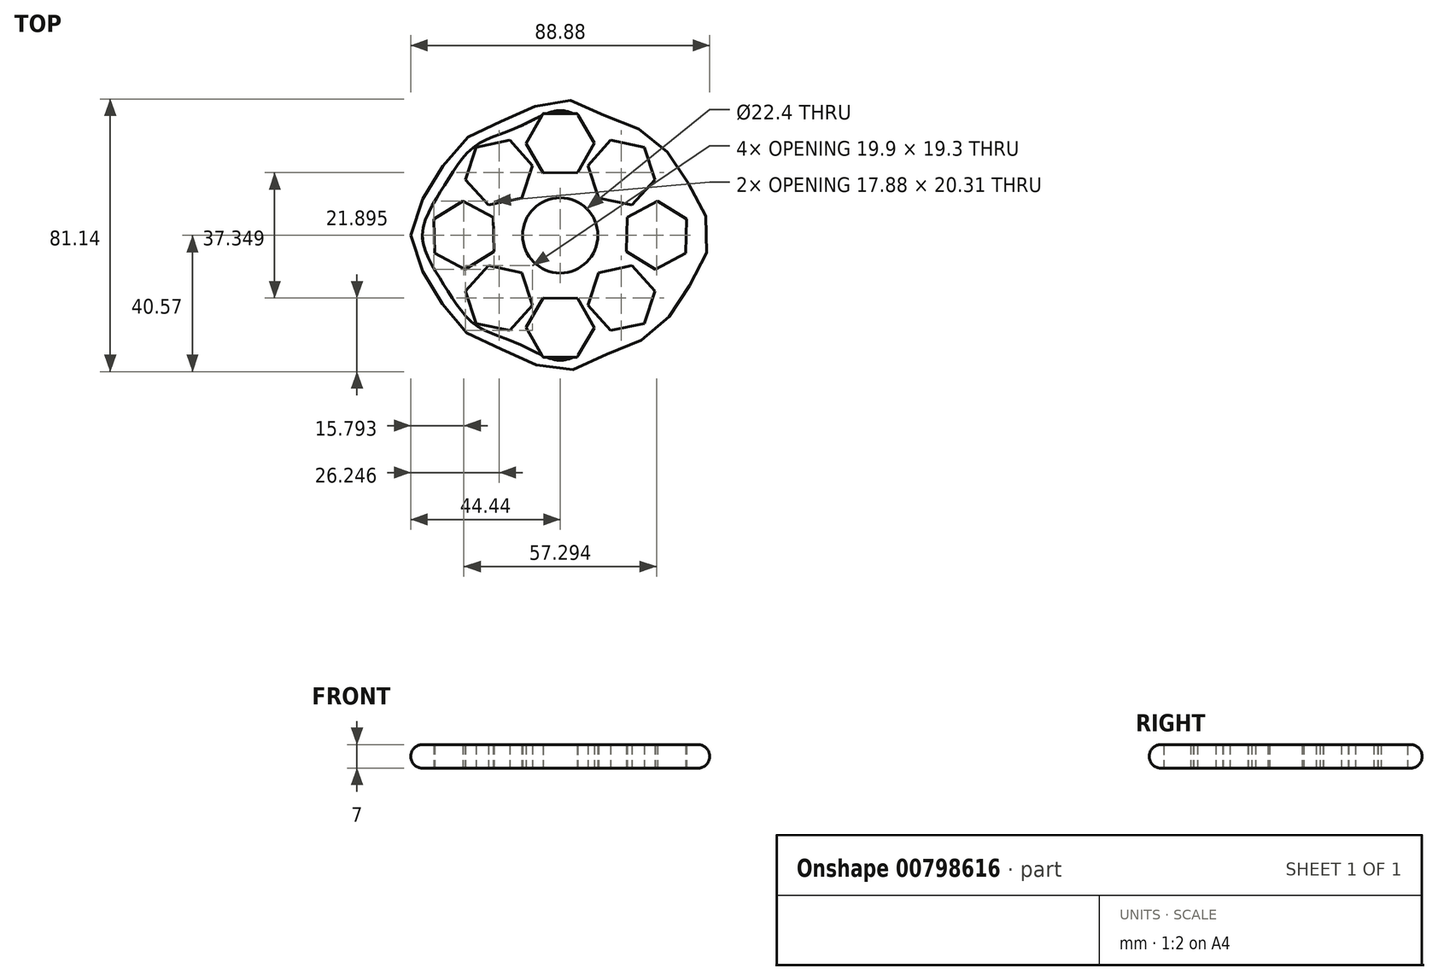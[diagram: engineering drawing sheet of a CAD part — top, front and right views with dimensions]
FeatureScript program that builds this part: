
annotation { "Feature Type Name" : "Feature", "Feature Type Description" : "" }
export const myFeature = defineFeature(function(context is Context, id is Id, definition is map)
    precondition{}
    {
        {
            var Q0;
            Q0=qCreatedBy(makeId("Top.planeOp"),FACE);
            var sketch = newSketch(context, id + "F0", { "sketchPlane" : qUnion([Q0])});
            skCircle(sketch, "E0", {"center": v(0, 0) * mm, "radius": 11.2 * mm});
            skCircle(sketch, "E1.cCircle", {"center": v(0, 27.46) * mm, "radius": 8.8 * mm});
            skLineSegment(sketch, "E1.0", {"start": v(10.16, 27.52) * mm, "end": v(5.14, 18.69) * mm});
            skLineSegment(sketch, "E1.1", {"start": v(5.14, 18.69) * mm, "end": v(-5.02, 18.62) * mm});
            skLineSegment(sketch, "E1.2", {"start": v(-5.02, 18.62) * mm, "end": v(-10.16, 27.4) * mm});
            skLineSegment(sketch, "E1.3", {"start": v(-10.16, 27.4) * mm, "end": v(-5.14, 36.22) * mm});
            skLineSegment(sketch, "E1.4", {"start": v(-5.14, 36.22) * mm, "end": v(5.02, 36.29) * mm});
            skLineSegment(sketch, "E1.5", {"start": v(5.02, 36.29) * mm, "end": v(10.16, 27.52) * mm});
            skCircle(sketch, "E2.MirrorC", {"center": v(0, -27.46) * mm, "radius": 8.8 * mm, "construction": true});
            skLineSegment(sketch, "E3.MirrorCS", {"start": v(-5.02, -18.62) * mm, "end": v(-10.16, -27.4) * mm});
            skLineSegment(sketch, "E4.MirrorCS", {"start": v(-10.16, -27.4) * mm, "end": v(-5.14, -36.22) * mm});
            skLineSegment(sketch, "E5.MirrorCS", {"start": v(-5.14, -36.22) * mm, "end": v(5.02, -36.29) * mm});
            skLineSegment(sketch, "E6.MirrorCS", {"start": v(5.02, -36.29) * mm, "end": v(10.16, -27.52) * mm});
            skLineSegment(sketch, "E7.MirrorCS", {"start": v(10.16, -27.52) * mm, "end": v(5.14, -18.69) * mm});
            skLineSegment(sketch, "E8.MirrorCS", {"start": v(5.14, -18.69) * mm, "end": v(-5.02, -18.62) * mm});
            skCircle(sketch, "E9.cCircle", {"center": v(28.65, 0) * mm, "radius": 8.8 * mm, "construction": true});
            skLineSegment(sketch, "E9.0", {"start": v(28.93, 10.16) * mm, "end": v(37.59, 4.83) * mm});
            skLineSegment(sketch, "E9.1", {"start": v(37.59, 4.83) * mm, "end": v(37.3, -5.33) * mm});
            skLineSegment(sketch, "E9.2", {"start": v(37.3, -5.33) * mm, "end": v(28.36, -10.16) * mm});
            skLineSegment(sketch, "E9.3", {"start": v(28.36, -10.16) * mm, "end": v(19.7, -4.83) * mm});
            skLineSegment(sketch, "E9.4", {"start": v(19.7, -4.83) * mm, "end": v(20, 5.33) * mm});
            skLineSegment(sketch, "E9.5", {"start": v(20, 5.33) * mm, "end": v(28.93, 10.16) * mm});
            skCircle(sketch, "E10.MirrorC", {"center": v(-28.65, 0) * mm, "radius": 8.8 * mm});
            skLineSegment(sketch, "E11.MirrorCS", {"start": v(-19.7, -4.83) * mm, "end": v(-20, 5.33) * mm});
            skLineSegment(sketch, "E12.MirrorCS", {"start": v(-20, 5.33) * mm, "end": v(-28.93, 10.16) * mm});
            skLineSegment(sketch, "E13.MirrorCS", {"start": v(-28.93, 10.16) * mm, "end": v(-37.59, 4.83) * mm});
            skLineSegment(sketch, "E14.MirrorCS", {"start": v(-37.59, 4.83) * mm, "end": v(-37.3, -5.33) * mm});
            skLineSegment(sketch, "E15.MirrorCS", {"start": v(-37.3, -5.33) * mm, "end": v(-28.36, -10.16) * mm});
            skLineSegment(sketch, "E16.MirrorCS", {"start": v(-28.36, -10.16) * mm, "end": v(-19.7, -4.83) * mm});
            skCircle(sketch, "E17.cCircle", {"center": v(-18.2, 18.67) * mm, "radius": 8.8 * mm, "construction": true});
            skLineSegment(sketch, "E17.0", {"start": v(-24.96, 26.26) * mm, "end": v(-15, 28.32) * mm});
            skLineSegment(sketch, "E17.1", {"start": v(-15, 28.32) * mm, "end": v(-8.24, 20.74) * mm});
            skLineSegment(sketch, "E17.2", {"start": v(-8.24, 20.74) * mm, "end": v(-11.43, 11.1) * mm});
            skLineSegment(sketch, "E17.3", {"start": v(-11.43, 11.1) * mm, "end": v(-21.38, 9.03) * mm});
            skLineSegment(sketch, "E17.4", {"start": v(-21.38, 9.03) * mm, "end": v(-28.14, 16.6) * mm});
            skLineSegment(sketch, "E17.5", {"start": v(-28.14, 16.6) * mm, "end": v(-24.96, 26.26) * mm});
            skCircle(sketch, "E18.MirrorC", {"center": v(18.2, 18.67) * mm, "radius": 8.8 * mm, "construction": true});
            skLineSegment(sketch, "E19.MirrorCS", {"start": v(8.24, 20.74) * mm, "end": v(11.43, 11.1) * mm});
            skLineSegment(sketch, "E20.MirrorCS", {"start": v(11.43, 11.1) * mm, "end": v(21.38, 9.03) * mm});
            skLineSegment(sketch, "E21.MirrorCS", {"start": v(21.38, 9.03) * mm, "end": v(28.14, 16.6) * mm});
            skLineSegment(sketch, "E22.MirrorCS", {"start": v(28.14, 16.6) * mm, "end": v(24.96, 26.26) * mm});
            skLineSegment(sketch, "E23.MirrorCS", {"start": v(24.96, 26.26) * mm, "end": v(15, 28.32) * mm});
            skLineSegment(sketch, "E24.MirrorCS", {"start": v(15, 28.32) * mm, "end": v(8.24, 20.74) * mm});
            skCircle(sketch, "E25.MirrorC", {"center": v(-18.2, -18.67) * mm, "radius": 8.8 * mm, "construction": true});
            skLineSegment(sketch, "E26.MirrorCS", {"start": v(-11.43, -11.1) * mm, "end": v(-21.38, -9.03) * mm});
            skLineSegment(sketch, "E27.MirrorCS", {"start": v(-21.38, -9.03) * mm, "end": v(-28.14, -16.6) * mm});
            skLineSegment(sketch, "E28.MirrorCS", {"start": v(-28.14, -16.6) * mm, "end": v(-24.96, -26.26) * mm});
            skLineSegment(sketch, "E29.MirrorCS", {"start": v(-24.96, -26.26) * mm, "end": v(-15, -28.32) * mm});
            skLineSegment(sketch, "E30.MirrorCS", {"start": v(-15, -28.32) * mm, "end": v(-8.24, -20.74) * mm});
            skLineSegment(sketch, "E31.MirrorCS", {"start": v(-8.24, -20.74) * mm, "end": v(-11.43, -11.1) * mm});
            skCircle(sketch, "E32.MirrorC", {"center": v(18.2, -18.67) * mm, "radius": 8.8 * mm, "construction": true});
            skLineSegment(sketch, "E33.MirrorCS", {"start": v(8.24, -20.74) * mm, "end": v(11.43, -11.1) * mm});
            skLineSegment(sketch, "E34.MirrorCS", {"start": v(15, -28.32) * mm, "end": v(8.24, -20.74) * mm});
            skLineSegment(sketch, "E35.MirrorCS", {"start": v(24.96, -26.26) * mm, "end": v(15, -28.32) * mm});
            skLineSegment(sketch, "E36.MirrorCS", {"start": v(28.14, -16.6) * mm, "end": v(24.96, -26.26) * mm});
            skLineSegment(sketch, "E37.MirrorCS", {"start": v(21.38, -9.03) * mm, "end": v(28.14, -16.6) * mm});
            skLineSegment(sketch, "E38.MirrorCS", {"start": v(11.43, -11.1) * mm, "end": v(21.38, -9.03) * mm});
            skPoint(sketch, "E39", {"position": v(-44.44, 0) * mm});
            skPoint(sketch, "E40", {"position": v(-37.84, 15.94) * mm});
            skPoint(sketch, "E41", {"position": v(-27.37, 29.3) * mm});
            skPoint(sketch, "E42", {"position": v(-13.69, 35.42) * mm});
            skPoint(sketch, "E43.MirrorP", {"position": v(37.84, 15.94) * mm});
            skPoint(sketch, "E44.MirrorP", {"position": v(44.44, 0) * mm});
            skPoint(sketch, "E45.MirrorP", {"position": v(27.37, 29.3) * mm});
            skPoint(sketch, "E46.MirrorP", {"position": v(13.69, 35.42) * mm});
            skPoint(sketch, "E47.MirrorP", {"position": v(-13.69, -35.42) * mm});
            skPoint(sketch, "E48.MirrorP", {"position": v(-27.37, -29.3) * mm});
            skPoint(sketch, "E49.MirrorP", {"position": v(-37.84, -15.94) * mm});
            skPoint(sketch, "E50.MirrorP", {"position": v(13.69, -35.42) * mm});
            skPoint(sketch, "E51.MirrorP", {"position": v(27.37, -29.3) * mm});
            skPoint(sketch, "E52.MirrorP", {"position": v(37.84, -15.94) * mm});
            skPoint(sketch, "E53", {"position": v(0, -40.57) * mm});
            skPoint(sketch, "E54.MirrorP", {"position": v(0, 40.57) * mm});
            skFitSpline(sketch, "E55", {"points": [v(-44.44, 0) * mm, v(-37.84, 15.94) * mm, v(-27.37, 29.3) * mm, v(-13.69, 35.42) * mm, v(0, 40.57) * mm, v(13.69, 35.42) * mm, v(27.37, 29.3) * mm, v(37.84, 15.94) * mm, v(44.44, 0) * mm, v(37.84, -15.94) * mm, v(27.37, -29.3) * mm, v(13.69, -35.42) * mm, v(0, -40.57) * mm, v(-13.69, -35.42) * mm, v(-27.37, -29.3) * mm, v(-37.84, -15.94) * mm, v(-44.44, 0) * mm]});
            skSolve(sketch);
        }
        {
            var Q0;
            Q0 = qSketchRegion(id + "F0", true);
            extrude(context, id + "F1", {"entities" : qUnion([Q0]), "depth" : 7 * mm, "offsetDistance" : 25.4 * mm});
        }
        {
            var Q0;
            Q0=makeQuery(id+"F1.opExtrude","CAP_EDGE",EDGE,{"disambiguationData":[OSD([sQuery(id+"F0.wireOp",EDGE,"E55")])],"isStart":true});
            var Q1;
            Q1=makeQuery(id+"F1.opExtrude","CAP_EDGE",EDGE,{"disambiguationData":[OSD([sQuery(id+"F0.wireOp",EDGE,"E55")])],"isStart":false});
            fillet(context, id + "F2", {"entities" : qUnion([Q0, Q1]), "radius" : 3.4 * mm, "tangentPropagation" : true, "allowEdgeOverflow" : false});
        }
    });
